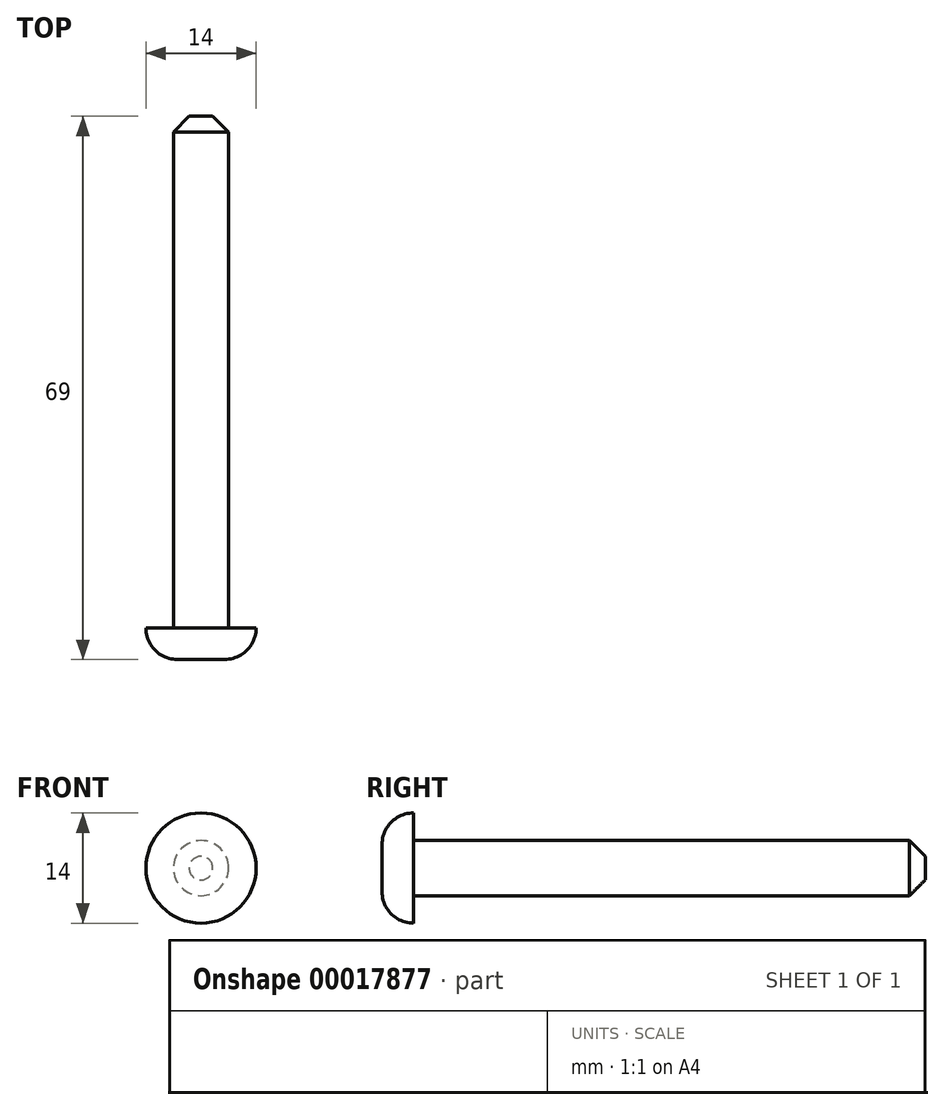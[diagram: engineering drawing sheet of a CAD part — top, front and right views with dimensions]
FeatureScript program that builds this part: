
annotation { "Feature Type Name" : "Feature", "Feature Type Description" : "" }
export const myFeature = defineFeature(function(context is Context, id is Id, definition is map)
    precondition{}
    {
        {
            var Q0;
            Q0=qCreatedBy(makeId("Front.planeOp"),FACE);
            var sketch = newSketch(context, id + "F0", { "sketchPlane" : qUnion([Q0])});
            skCircle(sketch, "E0", {"center": v(0, 0) * mm, "radius": 3.5 * mm});
            skSolve(sketch);
        }
        {
            var Q0;
            Q0=makeQuery(id+"F0.imprint","IMPRINT",FACE,{"disambiguationData":[TD([[makeQuery(id+"F0.imprint","IMPRINT",EDGE,{"derivedFrom":sQuery(id+"F0.wireOp",EDGE,"E0")}),1.0]])]});
            extrude(context, id + "F1", {"entities" : qUnion([Q0]), "depth" : 65 * mm});
        }
        {
            var Q0;
            Q0=makeQuery(id+"F1.opExtrude","CAP_FACE",FACE,{"disambiguationData":[OSD([sQuery(id+"F0.wireOp",EDGE,"E0")])],"isStart":false});
            var sketch = newSketch(context, id + "F2", { "sketchPlane" : qUnion([Q0])});
            skCircle(sketch, "E1", {"center": v(0, 0) * mm, "radius": 7 * mm});
            skSolve(sketch);
        }
        {
            var Q0;
            Q0 = qSketchRegion(id + "F2", true);
            extrude(context, id + "F3", {"entities" : qUnion([Q0]), "operationType" : NewBodyOperationType.ADD, "depth" : 4 * mm});
        }
        {
            var Q0;
            Q0=makeQuery(id+"F3.opExtrude","CAP_FACE",FACE,{"disambiguationData":[OSD([sQuery(id+"F2.wireOp",EDGE,"E1")])],"isStart":false});
            fillet(context, id + "F4", {"entities" : qUnion([Q0]), "radius" : 4 * mm, "tangentPropagation" : true, "allowEdgeOverflow" : false});
        }
        {
            var Q0;
            Q0=makeQuery(id+"F1.opExtrude","CAP_EDGE",EDGE,{"disambiguationData":[OSD([sQuery(id+"F0.wireOp",EDGE,"E0")])],"isStart":true});
            chamfer(context, id + "F5", {"entities" : qUnion([Q0]), "width" : 2 * mm, "tangentPropagation" : true});
        }
    });
